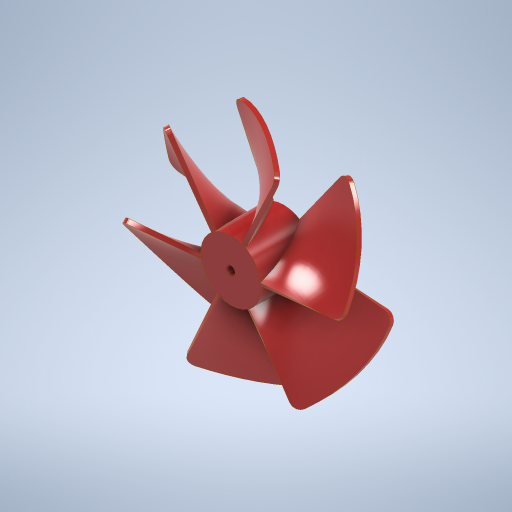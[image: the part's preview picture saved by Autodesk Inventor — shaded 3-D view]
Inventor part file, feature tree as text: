
AUTODESK INVENTOR PART (.ipt)
format: ipt  version: 2023 (Build 270158000, 158)  size: 1,532,928 bytes
history: native  units: mm
features: other x10, sketch x8, extrude x2, fillet x1, pattern_circular x1
ambient origin geometry x8: Origin, YZ Plane, XZ Plane, XY Plane, X Axis, Y Axis, Z Axis, Center Point
bodies: Body1 (feature_tree), Body2 (feature_tree), Body3 (feature_tree), Body4 (feature_tree), Body5 (feature_tree), Body6 (feature_tree), Body7 (feature_tree), Body8 (feature_tree), Body9 (feature_tree), Body10 (feature_tree), Body11 (feature_tree), Body12 (feature_tree), Body13 (feature_tree), Body14 (feature_tree), Body15 (feature_tree), Body16 (feature_tree), Body17 (feature_tree), Body18 (feature_tree), Body19 (feature_tree), Body20 (feature_tree), Body21 (feature_tree)
feature tree (22):
  other  "솔리드1"
  extrude  "돌출1"  Depth=15.0mm
  sketch  "스케치2"
  sketch  "스케치3"
  sketch  "3D 스케치1"
  other  "두껍게 하기1"
  fillet  "모깎기1"  Radius=13.0mm
  pattern_circular  "원형 패턴1"  [2 undecoded]
  other  "결합1"
  extrude  "돌출2"  Depth=4.363323mm
  sketch  "스케치1"
  other  "곡면에 투영1"
  sketch  "스케치4"
  other  "Srf1"
  sketch  "3D 스케치2"
  other  "곡면에 투영2"
  sketch  "3D 스케치3"
  other  "Srf2"
  other  "솔리드2"
  sketch  "스케치5"
  other  "돌출 곡면1"
  other  "경계 패치1"
note: 2 required parameter values undecoded (feature->parameter linkage not recoverable at this tier; creation-order binding heuristic only, values carry confidence <= 0.55)
